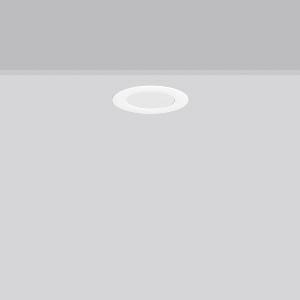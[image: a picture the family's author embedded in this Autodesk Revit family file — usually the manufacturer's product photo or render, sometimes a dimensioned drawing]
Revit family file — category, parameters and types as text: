
# Revit family: toledo_flat_round_e_901451_002_4028
name_source: partatom
category: Lighting Fixtures
units: mm (PartAtom-declared; Revit-internal decimal feet)

## family parameters
Cut with Voids When Loaded = No
Host = Face
Light Source = No
Part Type = Normal
Room Calculation Point = No
Round Connector Dimension = Use Diameter
Shared = No

## types (1)
- TOLEDO FLAT round E (1 x LED Modul 830, 470 lm, 3000)
    Apparent Load = 5 VA
    CIE Flux Codes = 48 79 96 100 100
    Color Rendering = 80
    Color Temperature = 3000
    Default Elevation = 1800 mm
    Description = Series: TOLEDO FLAT round
Ultra thin recessed downlight. Housing: die-cast aluminium. Light guide and diffuser made of non-yellowing PMMA, opal matt. Ceiling installation with spring system. Mounting depth depends on ceiling strength. Including separate LED converter with connecting cable 250 mm. Suitable for through-wiring with separately available accessories. Surface mounted housing as accessory for all sizes. Retrofittable decorative cylinders made of chintz fabric as accessory, optional with satin finish plastic diffuser. Through-wiring box (5 pole) available as accessory. 
Colour: white
Diameter: 148 mm
Height: 2 mm
Cut-out diameter: 128 mm
Recess height: 27-53 mm
Luminaire: recess height: 31-51 mm
Lamp: LED
Socket: without socket
Colour temperature: 3000K
Colour rendering index (CRI): 80
System power: 5 W
Rated luminous flux: 470 lm
Luminous efficiency: 94 lm/W
Control gear: Regulated power supply
Protection class: II
Type of protection: IP 54
    Height = 0 mm  [stored 0 ft]
    Lamp = 1 x LED Modul 830
    Lamp Light Flux = 470 lm
    Lamp count = 1
    Length = 148 mm
    Lifetime = 50000 h
    Luminous efficacy = 94 lm/W
    Manufacturer = RZB
    ModVariant = No
    Model = 901451.002
    Mounting Place = Ceiling
    Mounting Type = Recessed
    Number of Poles = 1
    OnlyDefault = Yes
    Power Factor = 1
    Product Name = TOLEDO FLAT round E
    Product group = Recessed downlights
    ProductGroupID = 402
    Protection Class = Protection class II
    Protection Degree = IP 20
    RLX_Detail_Level = 1
    RLX_Emergency_Light_Flux = 0 lm
    RLX_Emergency_Type = 0
    RLX_Emergency_Type_DB = No
    RlxData = <blob elided: 74625 chars, md5=dc4db03b>
    Socket = socket
    Standby Power = 0 W
    System Light Flux = 470 lm
    System Power = 5 W
    Type Comments = Product without accessories
    Type Image = 901451.002.jpg
    URL = http://relux.com
    VarID = ---
    Voltage = 230 V
    Voltage Range = 220-240 V
    Weight = 0.00 kg
    Width = 0 mm  [stored 0 ft]

note: [stored X ft] marks values corroborated as IEEE doubles in the binary element streams (Revit-internal decimal feet)

## geometry (parser evidence)
native form markers: Blend x4, Sweep x10
no freeform markers — native parametric forms only
